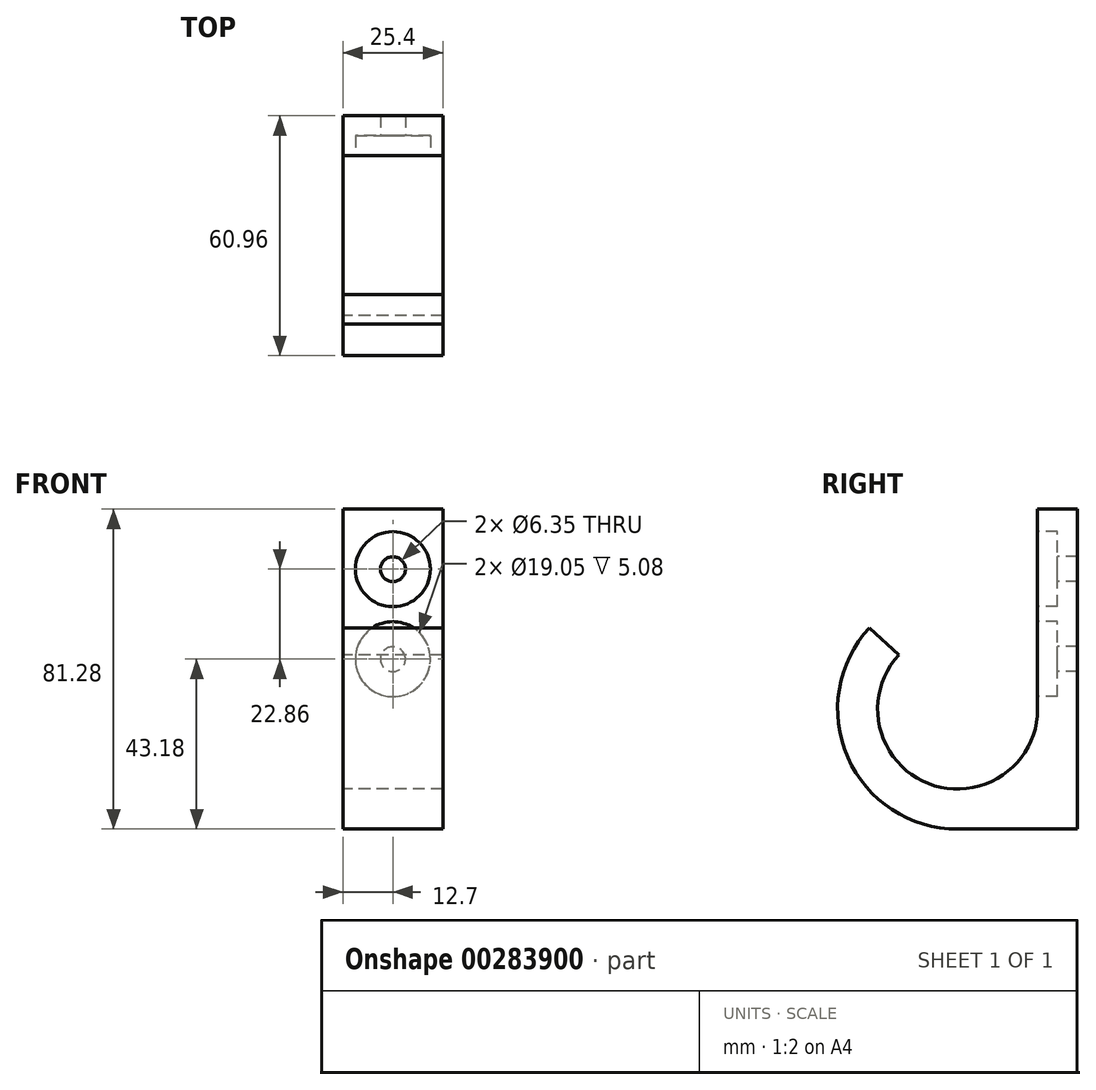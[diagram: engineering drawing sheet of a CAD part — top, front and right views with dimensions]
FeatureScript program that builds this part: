
annotation { "Feature Type Name" : "Feature", "Feature Type Description" : "" }
export const myFeature = defineFeature(function(context is Context, id is Id, definition is map)
    precondition{}
    {
        {
            var Q0;
            Q0=qCreatedBy(makeId("Right.planeOp"),FACE);
            var sketch = newSketch(context, id + "F0", { "sketchPlane" : qUnion([Q0])});
            skLineSegment(sketch, "E0", {"start": v(0, 0) * mm, "end": v(0, 50.8) * mm});
            skArc(sketch, "E1", {"start": v(0, 0) * mm, "mid": v(-20.32, -20.32) * mm, "end": v(-40.64, 0) * mm});
            skArc(sketch, "E2", {"start": v(-40.64, 0) * mm, "mid": v(-39.25, 7.4) * mm, "end": v(-35.26, 13.78) * mm});
            skArc(sketch, "E3.0", {"start": v(-50.8, 0) * mm, "mid": v(-48.7, 11.1) * mm, "end": v(-42.73, 20.66) * mm});
            skArc(sketch, "E3.1", {"start": v(10.16, 0) * mm, "mid": v(-20.32, -30.48) * mm, "end": v(-50.8, 0) * mm});
            skLineSegment(sketch, "E3.2", {"start": v(10.16, 0) * mm, "end": v(10.16, 50.8) * mm});
            skLineSegment(sketch, "E4", {"start": v(-20.32, 0) * mm, "end": v(-20.32, -30.48) * mm, "construction": true});
            skLineSegment(sketch, "E5", {"start": v(10.16, 0) * mm, "end": v(10.16, -30.48) * mm});
            skLineSegment(sketch, "E6", {"start": v(10.16, -30.48) * mm, "end": v(-20.32, -30.48) * mm});
            skLineSegment(sketch, "E7", {"start": v(-42.73, 20.66) * mm, "end": v(-35.26, 13.78) * mm});
            skLineSegment(sketch, "E8", {"start": v(0, 50.8) * mm, "end": v(10.16, 50.8) * mm});
            skSolve(sketch);
        }
        {
            var Q0;
            Q0 = qSketchRegion(id + "F0", true);
            extrude(context, id + "F1", {"entities" : qUnion([Q0]), "endBound" : BoundingType.SYMMETRIC, "depth" : 25.4 * mm});
        }
        {
            var Q0;
            Q0=makeQuery(id+"F1.opExtrude","SWEPT_FACE",FACE,{"disambiguationData":[OSD([sQuery(id+"F0.wireOp",EDGE,"E0")])]});
            var sketch = newSketch(context, id + "F2", { "sketchPlane" : qUnion([Q0])});
            skLineSegment(sketch, "E9", {"start": v(0, 0) * mm, "end": v(0, 12.7) * mm, "construction": true});
            skCircle(sketch, "E10", {"center": v(0, 12.7) * mm, "radius": 3.18 * mm});
            skCircle(sketch, "E11", {"center": v(0, 35.56) * mm, "radius": 3.18 * mm});
            skCircle(sketch, "E12.0", {"center": v(0, 35.56) * mm, "radius": 9.52 * mm});
            skCircle(sketch, "E13.0", {"center": v(0, 12.7) * mm, "radius": 9.52 * mm});
            skSolve(sketch);
        }
        {
            var Q0;
            Q0=makeQuery(id+"F2.imprint","IMPRINT",FACE,{"disambiguationData":[TD([[makeQuery(id+"F2.imprint","IMPRINT",EDGE,{"derivedFrom":sQuery(id+"F2.wireOp",EDGE,"E11")}),1.0]])]});
            var Q1;
            Q1=makeQuery(id+"F2.imprint","IMPRINT",FACE,{"disambiguationData":[TD([[makeQuery(id+"F2.imprint","IMPRINT",EDGE,{"derivedFrom":sQuery(id+"F2.wireOp",EDGE,"E10")}),1.0]])]});
            extrude(context, id + "F3", {"entities" : qUnion([Q0, Q1]), "operationType" : NewBodyOperationType.REMOVE, "endBound" : BoundingType.THROUGH_ALL, "oppositeDirection" : true, "depth" : 25.4 * mm});
        }
        {
            var Q0;
            Q0 = qSketchRegion(id + "F2", true);
            extrude(context, id + "F4", {"entities" : qUnion([Q0]), "operationType" : NewBodyOperationType.REMOVE, "oppositeDirection" : true, "depth" : 5.08 * mm});
        }
    });
